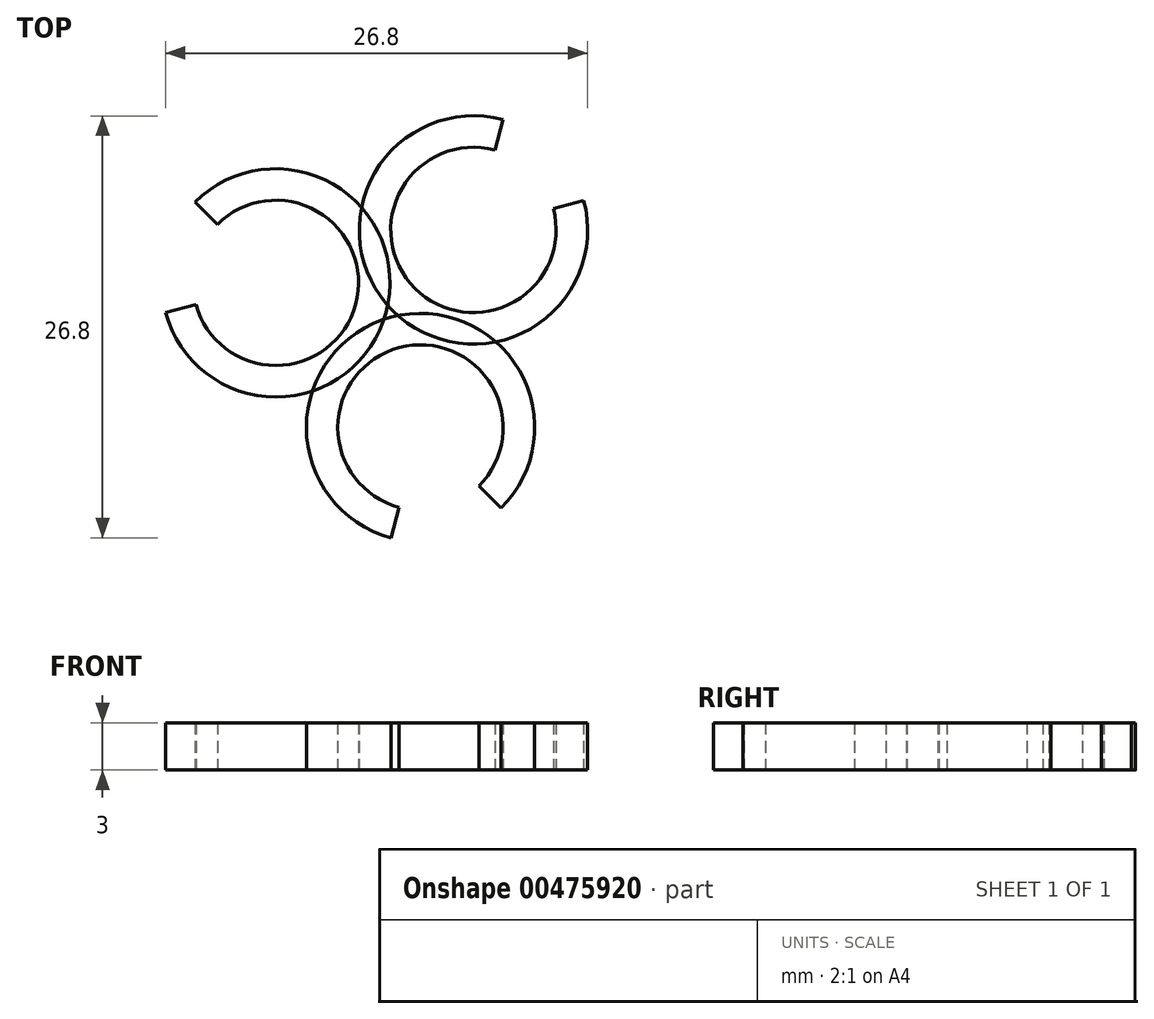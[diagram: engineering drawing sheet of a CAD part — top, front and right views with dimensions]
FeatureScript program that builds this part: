
annotation { "Feature Type Name" : "Feature", "Feature Type Description" : "" }
export const myFeature = defineFeature(function(context is Context, id is Id, definition is map)
    precondition{}
    {
        {
            assignVariable(context, id + "F0", {"name" : "holderHeight", "anyValue" : 3});
        }
        {
            assignVariable(context, id + "F1", {"name" : "elementCount", "anyValue" : 2});
        }
        {
            assignVariable(context, id + "F2", {"name" : "elementCount", "anyValue" : 3});
        }
        {
            var Q0;
            Q0=qCreatedBy(makeId("Top.planeOp"),FACE);
            var sketch = newSketch(context, id + "F3", { "sketchPlane" : qUnion([Q0])});
            skCircle(sketch, "E0", {"center": v(5.3, 5.3) * mm, "radius": 5.25 * mm});
            skCircle(sketch, "E1.0", {"center": v(5.3, 5.3) * mm, "radius": 7.5 * mm, "construction": true});
            skLineSegment(sketch, "E2", {"start": v(5.3, 5.3) * mm, "end": v(0, 5.3) * mm, "construction": true});
            skLineSegment(sketch, "E3", {"start": v(5.3, 5.3) * mm, "end": v(5.3, 0) * mm, "construction": true});
            skCircle(sketch, "E4.0", {"center": v(5.3, 5.3) * mm, "radius": 7.25 * mm});
            skLineSegment(sketch, "E5", {"start": v(5.3, 5.3) * mm, "end": v(7.18, 12.3) * mm, "construction": true});
            skLineSegment(sketch, "E6", {"start": v(5.3, 5.3) * mm, "end": v(12.3, 7.18) * mm, "construction": true});
            skLineSegment(sketch, "E7", {"start": v(0, 0) * mm, "end": v(10.43, 10.43) * mm, "construction": true});
            skPoint(sketch, "E8", {"position": v(6.66, 10.37) * mm});
            skPoint(sketch, "E9", {"position": v(10.37, 6.66) * mm});
            skLineSegment(sketch, "E10", {"start": v(7.18, 12.3) * mm, "end": v(6.66, 10.37) * mm});
            skLineSegment(sketch, "E11", {"start": v(10.37, 6.66) * mm, "end": v(12.3, 7.18) * mm});
            skSolve(sketch);
        }
        {
            var Q0;
            {var subQ0=sQuery(id+"F3.wireOp",EDGE,"E10");Q0=makeQuery(id+"F3.imprint","IMPRINT",FACE,{"disambiguationData":[TD([[makeQuery(id+"F3.imprint","IMPRINT",EDGE,{"derivedFrom":subQ0}),-1.0]])]});}
            extrude(context, id + "F4", {"entities" : qUnion([Q0]), "depth" : (getVariable(context, 'holderHeight')) * mm, "offsetDistance" : 25 * mm});
        }
        {
            var Q0;
            Q0=qCreatedBy(makeId("Right.planeOp"),FACE);
            var sketch = newSketch(context, id + "F5", { "sketchPlane" : qUnion([Q0])});
            skLineSegment(sketch, "E12", {"start": v(0, 35.85) * mm, "end": v(0, -33.62) * mm, "construction": true});
            skSolve(sketch);
        }
        {
            var Q0;
            Q0=makeQuery(id+"F4.opExtrude","SWEPT_BODY",BODY,{"disambiguationData":[OSD([sQuery(id+"F3.wireOp",EDGE,"E0"),sQuery(id+"F3.wireOp",EDGE,"E4.0"),sQuery(id+"F3.wireOp",EDGE,"E10"),sQuery(id+"F3.wireOp",EDGE,"E11")])]});
            var Q1;
            Q1=sQuery(id+"F5.wireOp",EDGE,"E12");
            circularPattern(context, id + "F6", {"entities" : qUnion([Q0]), "axis" : qUnion([Q1]), "angle" : 360 * degree, "instanceCount" : getVariable(context, 'elementCount'), "equalSpace" : true});
        }
    });
